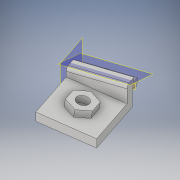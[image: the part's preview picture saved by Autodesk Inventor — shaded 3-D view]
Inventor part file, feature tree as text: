
AUTODESK INVENTOR PART (.ipt)
format: ipt  version: 2018 (Build 220112000, 112)  size: 191,488 bytes
history: native  units: in
note: dims shown in document units (in); Inventor stores cm internally (conversion verified against a paired STEP export)
features: extrude x7, sketch x7, plane x3, fillet x1
ambient origin geometry x8: Origin, YZ Plane, XZ Plane, XY Plane, X Axis, Y Axis, Z Axis, Center Point
bodies: Solid1 (feature_tree)
feature tree (18):
  plane  "Work Plane2"
  extrude  "Extrusion2"  Depth=0.1969in
  plane  "Work Plane4"
  extrude  "Extrusion4"  Depth=0.0787in
  extrude  "Extrusion6"  Depth=1.1811in TaperAngle=0.0deg
  fillet  "Fillet2"  Radius=0.1181in
  extrude  "Extrusion7"  [1 undecoded]
  plane  "Work Plane7"
  extrude  "Extrusion8"  Depth=0.0197in
  extrude  "Extrusion9"  Depth=0.1181in
  extrude  "Extrusion10"  Depth=0.1673in
  sketch  "Sketch3"  dims[d5=0.1969in d6=0.1969in]
  sketch  "Sketch5"  dims[d7=0.0787in d9=1.0994in]
  sketch  "Sketch7"  dims[d12=0.1378in d13=1.1811in d14=0.0in d20=0.1181in]
  sketch  "Sketch8"  dims[d21=0.1772in d23=-0.1772in]
  sketch  "Sketch10"  dims[d24=0.0197in d25=0.5906in]
  sketch  "Sketch11"  dims[d26=0.0984in d27=0.1181in]
  sketch  "Sketch13"  dims[d28=0.3937in d29=0.0in d34=0.1374in d35=0.1969in d36=1.5748in d37=0.0in d38=0.0in d39=0.0197in d40=0.7874in d41=0.0in d48=-0.1969in d49=1.1811in d50=0.1969in d51=0.1969in d52=0.1969in d53=0.0in d54=0.1969in d55=1.1811in d56=0.0in d57=0.5906in d58=0.5315in d59=0.2756in d60=0.1673in d61=0.0in]
note: 1 required parameter value undecoded (feature->parameter linkage not recoverable at this tier; creation-order binding heuristic only, values carry confidence <= 0.55)
